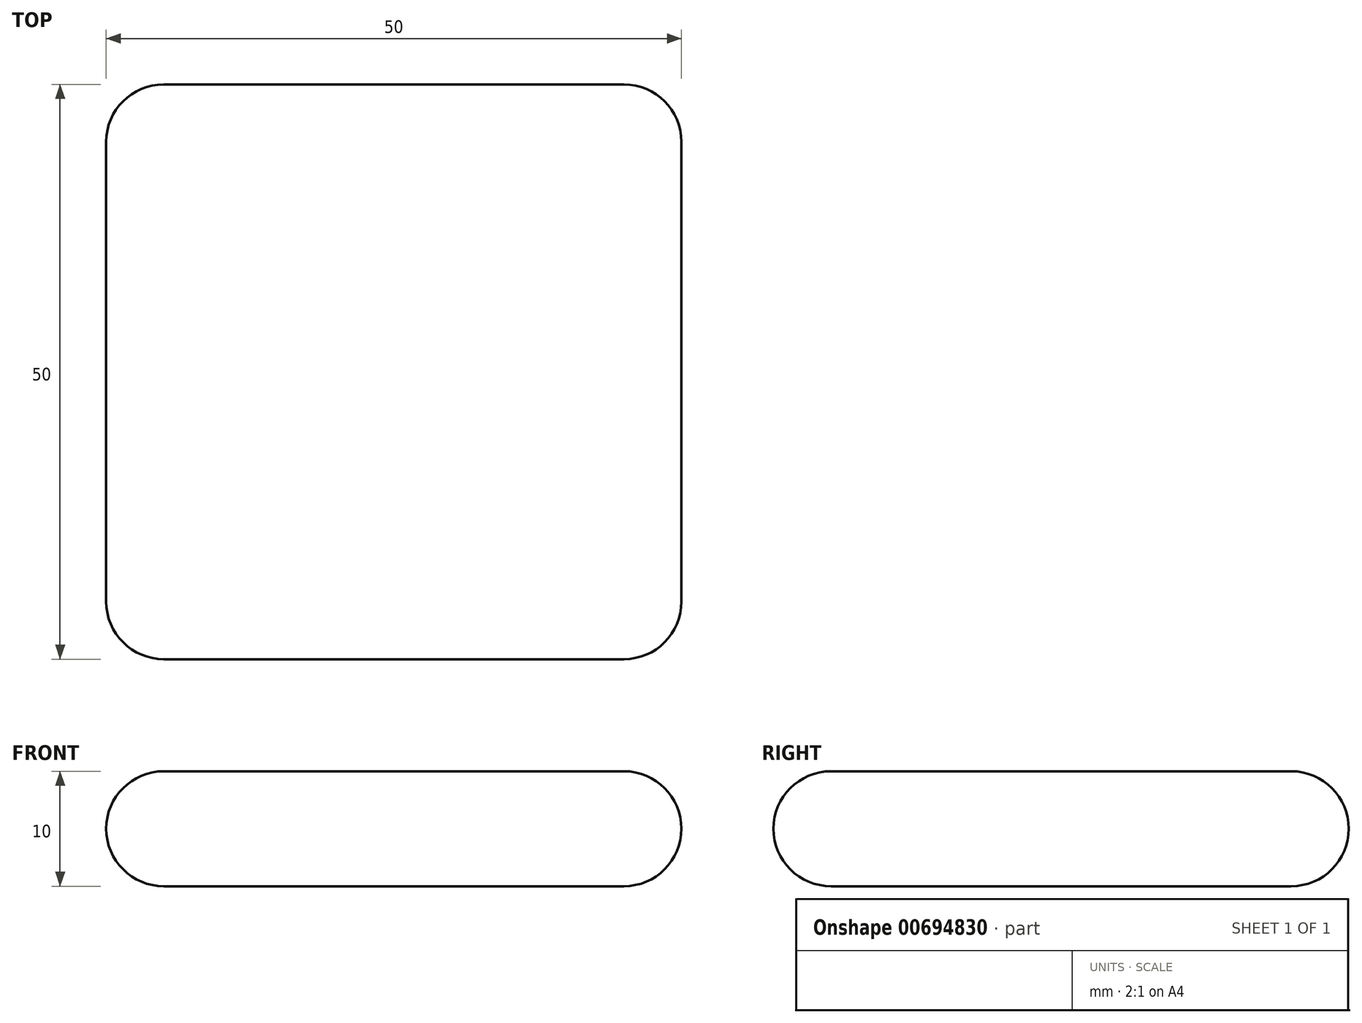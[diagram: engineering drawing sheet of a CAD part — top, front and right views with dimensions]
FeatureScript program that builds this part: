
annotation { "Feature Type Name" : "Feature", "Feature Type Description" : "" }
export const myFeature = defineFeature(function(context is Context, id is Id, definition is map)
    precondition{}
    {
        {
            var Q0;
            Q0=qCreatedBy(makeId("Top.planeOp"),FACE);
            var sketch = newSketch(context, id + "F0", { "sketchPlane" : qUnion([Q0])});
            skLineSegment(sketch, "E0.bottom", {"start": v(25, -25) * mm, "end": v(-25, -25) * mm});
            skLineSegment(sketch, "E0.top", {"start": v(25, 25) * mm, "end": v(-25, 25) * mm});
            skLineSegment(sketch, "E0.left", {"start": v(25, -25) * mm, "end": v(25, 25) * mm});
            skLineSegment(sketch, "E0.right", {"start": v(-25, -25) * mm, "end": v(-25, 25) * mm});
            skPoint(sketch, "E0.middle", {"position": v(0, 0) * mm});
            skSolve(sketch);
        }
        {
            var Q0;
            Q0=makeQuery(id+"F0.imprint","IMPRINT",FACE,{"disambiguationData":[TD([[makeQuery(id+"F0.imprint","IMPRINT",EDGE,{"derivedFrom":sQuery(id+"F0.wireOp",EDGE,"E0.bottom")}),-1.0]])]});
            extrude(context, id + "F1", {"entities" : qUnion([Q0]), "depth" : 10 * mm, "offsetDistance" : 25 * mm});
        }
        {
            var Q0;
            Q0=makeQuery(id+"F1.opExtrude","CAP_EDGE",EDGE,{"disambiguationData":[OSD([sQuery(id+"F0.wireOp",EDGE,"E0.right")])],"isStart":false});
            var Q1;
            Q1=makeQuery(id+"F1.opExtrude","CAP_EDGE",EDGE,{"disambiguationData":[OSD([sQuery(id+"F0.wireOp",EDGE,"E0.right")])],"isStart":true});
            var Q2;
            Q2=makeQuery(id+"F1.opExtrude","CAP_EDGE",EDGE,{"disambiguationData":[OSD([sQuery(id+"F0.wireOp",EDGE,"E0.bottom")])],"isStart":true});
            var Q3;
            Q3=makeQuery(id+"F1.opExtrude","CAP_EDGE",EDGE,{"disambiguationData":[OSD([sQuery(id+"F0.wireOp",EDGE,"E0.bottom")])],"isStart":false});
            var Q4;
            Q4=makeQuery(id+"F1.opExtrude","SWEPT_EDGE",EDGE,{"disambiguationData":[OSD([sQuery(id+"F0.wireOp",EDGE,"E0.bottom"),sQuery(id+"F0.wireOp",EDGE,"E0.right")])]});
            var Q5;
            Q5=makeQuery(id+"F1.opExtrude","SWEPT_EDGE",EDGE,{"disambiguationData":[OSD([sQuery(id+"F0.wireOp",EDGE,"E0.bottom"),sQuery(id+"F0.wireOp",EDGE,"E0.left")])]});
            var Q6;
            Q6=makeQuery(id+"F1.opExtrude","CAP_EDGE",EDGE,{"disambiguationData":[OSD([sQuery(id+"F0.wireOp",EDGE,"E0.left")])],"isStart":false});
            var Q7;
            Q7=makeQuery(id+"F1.opExtrude","CAP_EDGE",EDGE,{"disambiguationData":[OSD([sQuery(id+"F0.wireOp",EDGE,"E0.left")])],"isStart":true});
            var Q8;
            Q8=makeQuery(id+"F1.opExtrude","CAP_EDGE",EDGE,{"disambiguationData":[OSD([sQuery(id+"F0.wireOp",EDGE,"E0.top")])],"isStart":true});
            var Q9;
            Q9=makeQuery(id+"F1.opExtrude","CAP_EDGE",EDGE,{"disambiguationData":[OSD([sQuery(id+"F0.wireOp",EDGE,"E0.top")])],"isStart":false});
            var Q10;
            Q10=makeQuery(id+"F1.opExtrude","SWEPT_EDGE",EDGE,{"disambiguationData":[OSD([sQuery(id+"F0.wireOp",EDGE,"E0.top"),sQuery(id+"F0.wireOp",EDGE,"E0.left")])]});
            var Q11;
            Q11=makeQuery(id+"F1.opExtrude","SWEPT_EDGE",EDGE,{"disambiguationData":[OSD([sQuery(id+"F0.wireOp",EDGE,"E0.top"),sQuery(id+"F0.wireOp",EDGE,"E0.right")])]});
            fillet(context, id + "F2", {"entities" : qUnion([Q0, Q1, Q2, Q3, Q4, Q5, Q6, Q7, Q8, Q9, Q10, Q11]), "radius" : 5 * mm, "tangentPropagation" : true, "allowEdgeOverflow" : false});
        }
    });
